# Revit family: QF_RATIONAL_CombiSteamer_iCP_XS_6-23E
name_source: partatom
category: Specialty Equipment
revit_build: Autodesk Revit 2018 (Build: 20170223_1515(x64)
units: mm (PartAtom-declared; Revit-internal decimal feet)

## family parameters
Always vertical = Yes
Cut with Voids When Loaded = No
OmniClass Number = 23.40.40.14.17.11
OmniClass Title = Cookers, Ovens, Stoves
Part Type = Normal
Room Calculation Point = No
Round Connector Dimension = Use Diameter
Shared = No
Work Plane-Based = No

## types (17) — shared parameters
Assembly Code = E1090320
Cold Water Flow = 0.1 L/s
Cold Water Maximum Pressure = 6.0 bar
Cold Water Minimum Pressure = 1.0 bar
Cold Water Size = 1"
Conn Conduit = Yes
Cycle = 50 Hz
Cycle Alternative = 60 Hz
Depth Actual = 22"
Description = Electrical Combi-steamer (6 x 2/3 GN)
Direct Waste Size = 2"
Exhaust Hood None = Hood : None
Height Actual = 30"
Hood UltraVent = Hood : UltraVent
Hood UltraVent Plus = Hood : UltraVent Plus
Integration Kit UltraVent = Accessories : UltraVent Integration Kit
Integration Kit UltraVent Plus = Accessories : UltraVent Plus Integration Kit
Latent Heat Output = 0 kW
Length Actual = 22 1/2"
Manufacturer = RATIONAL AG
Model = iCombi Pro XS 6-2/3
Sensitive Heat Output = 0 kW
Sound Level = 55dBA
Specification by Manufacturer = Hot-air steamer (combi-steamer mode) for most of the cooking methods used in commercial kitchens for the optional use of steam and hot-air, individually, in succession or in combination.
Stand None = Accessories : None
Stand UG I = Accessories : UG I 931
Stand UG II = Accessories : UG II 931
Stand UG XS = Accessories : UG XS 148
Stand Wall Mount = Accessories : Wall Mount
URL = www.rational-online.com
Version = 05-2020
Warranty Duration = 2 years
Waste Water Discharge Temperature = 65 °C
Weight = 66.00 kg

## per-type parameters (varying)
| type | FL Amps | Max Overcurrent Protection | Phase | Volts | Watts |
| XS 6-2/3E 1NAC 230V | 23 A | 25 A | 1 | 230 V | 5300 W |
| XS 6-2/3E 3NAC 380V Korea Version only | 9 A | 10 A | 3 | 380 V | 5300 W |
| XS 6-2/3E 3NAC 415V | 10 A | 10 A | 3 | 415 V | 6300 W |
| XS 6-2/3E 3NAC 400V - Marine Version only | 7 A | 10 A | 3 | 400 V | 5000 W |
| XS 6-2/3E 3NAC 400V | 9 A | 10 A | 3 | 400 V | 5000 W |
| XS 6-2/3E 3AC 240V | 16 A | 16 A | 3 | 240 V | 6300 W |
| XS 6-2/3E 3AC 230V | 15 A | 16 A | 3 | 230 V | 5300 W |
| XS 6-2/3E 3AC 220V - Marine Version only | 13 A | 16 A | 3 | 220 V | 5000 W |
| XS 6-2/3E 3AC 220V - Korea Version only | 14 A | 20 A | 3 | 220 V | 5300 W |
| XS 6-2/3E 3AC 208V | 16 A | 25 A | 3 | 208 V | 5700 W |
| XS 6-2/3E 3AC 200V | 16 A | 16 A | 3 | 200 V | 5300 W |
| XS 6-2/3E 2AC 240V | 24 A | 32 A | 2 | 240 V | 5700 W |
| XS 6-2/3E 2AC 230V | 23 A | 25 A | 2 | 230 V | 5300 W |
| XS 6-2/3E 2AC 208V | 27 A | 35 A | 2 | 208 V | 5700 W |
| XS 6-2/3E 1NAC 220 V - Korea Version only | 22 A | 25 A | 1 | 220 V | 5000 W |
| XS 6-2/3E 1NAC 240V | 24 A | 25 A | 1 | 240 V | 5700 W |
| XS 6-2/3E 3AC 220V | 14 A | 20 A | 3 | 220 V | 5300 W |

## geometry (parser evidence)
native form markers: Sweep x23
no freeform markers — native parametric forms only
